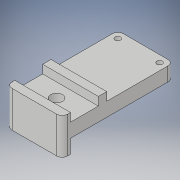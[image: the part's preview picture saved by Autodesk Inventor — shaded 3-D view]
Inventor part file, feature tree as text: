
AUTODESK INVENTOR PART (.ipt)
format: ipt  version: 2019 (Build 230136000, 136)  size: 177,152 bytes
history: native  units: in
note: dims shown in document units (in); Inventor stores cm internally (conversion verified against a paired STEP export)
features: sketch x7, extrude x6, hole x1, fillet x1, projected_geometry x1
ambient origin geometry x8: Origin, YZ Plane, XZ Plane, XY Plane, X Axis, Y Axis, Z Axis, Center Point
bodies: Solid1 (feature_tree)
feature tree (16):
  extrude  "Extrusion1"  Depth=0.7874in
  extrude  "Extrusion2"  Depth=0.1181in
  hole  "Hole1"  [1 undecoded]
  extrude  "Extrusion3"  Depth=0.315in
  extrude  "Extrusion5"  Depth=0.1575in TaperAngle=0.0deg
  extrude  "Extrusion6"  Depth=0.0787in
  sketch  "Sketch9"  dims[d28=0.0787in d29=0.0787in d30=0.0984in d31=0.0984in d32=0.0984in d33=0.3937in d34=0.0in d35=0.1969in d36=0.0in d37=0.0787in d38=0.0787in d39=0.0787in d40=0.0787in d41=0.0591in d42=0.0787in d43=0.1181in d44=0.0in]
  extrude  "Extrusion7"  Depth=0.0984in
  fillet  "Fillet2"  Radius=0.0984in
  sketch  "Sketch1"  dims[d0=0.1969in d1=0.0in d2=0.7874in]
  sketch  "Sketch2"  dims[d3=1.5748in d4=0.1181in]
  sketch  "Sketch3"  dims[d5=0.1181in d6=0.3937in]
  projected_geometry  "Projected Loop1"
  sketch  "Sketch4"  dims[d7=0.1181in d8=0.0in]
  sketch  "Sketch6"  dims[d9=0.1695in d10=0.2362in d11=0.279in d12=0.0787in d13=0.5635in d14=0.315in d15=0.8108in d16=0.3125in]
  sketch  "Sketch8"  dims[d17=0.6566in d18=0.1575in d19=0.0in]
note: 1 required parameter value undecoded (feature->parameter linkage not recoverable at this tier; creation-order binding heuristic only, values carry confidence <= 0.55)
